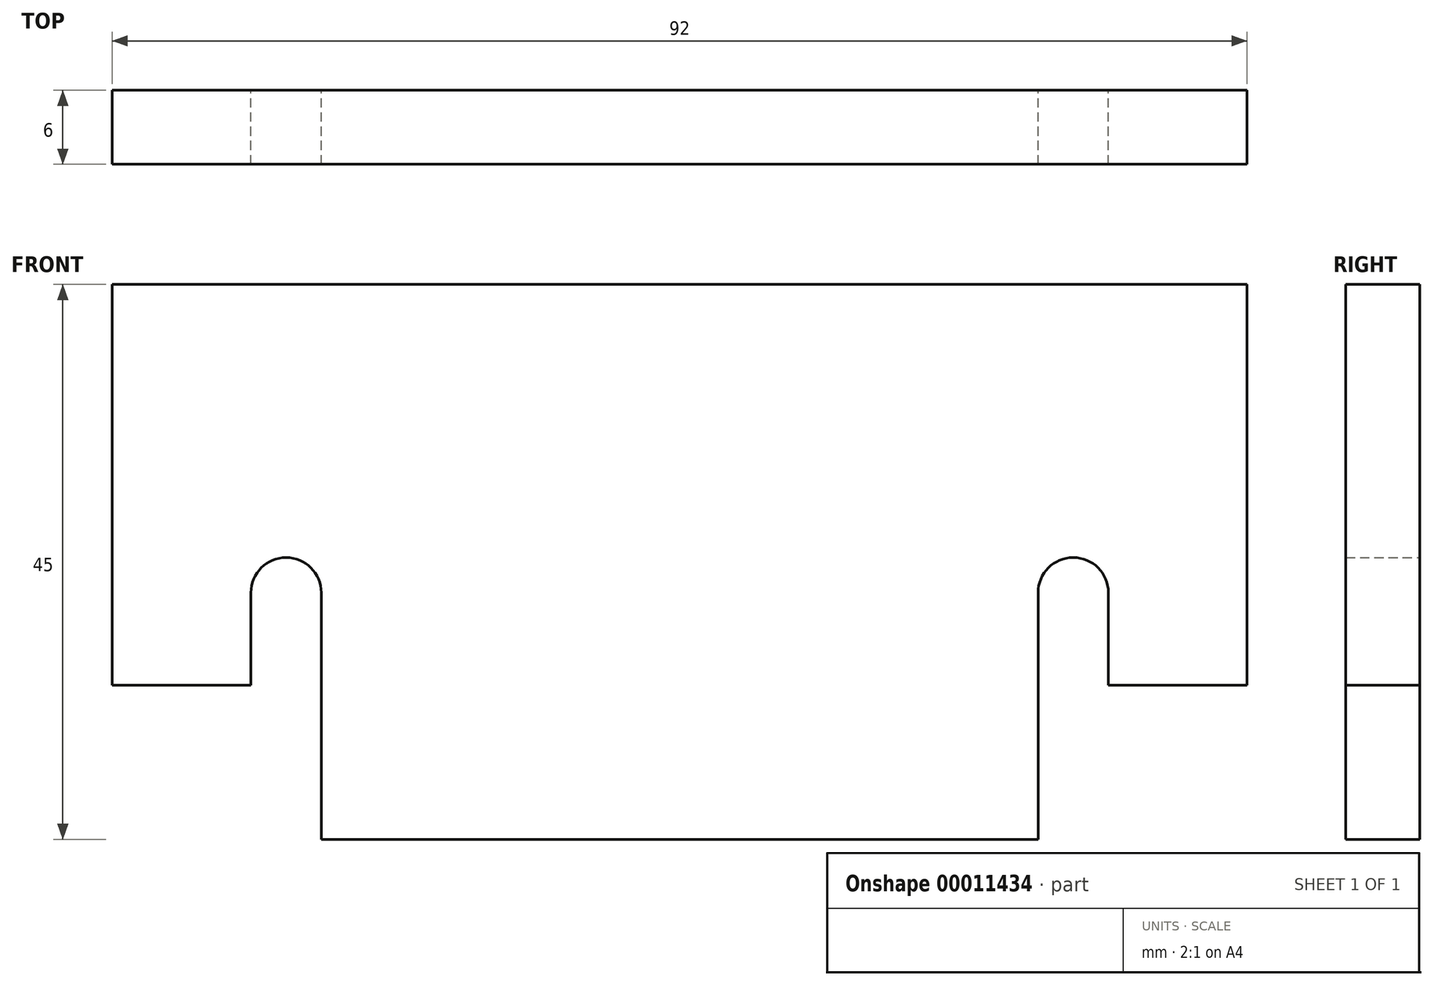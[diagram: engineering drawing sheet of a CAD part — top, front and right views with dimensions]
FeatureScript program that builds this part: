
annotation { "Feature Type Name" : "Feature", "Feature Type Description" : "" }
export const myFeature = defineFeature(function(context is Context, id is Id, definition is map)
    precondition{}
    {
        {
            var Q0;
            Q0=qCreatedBy(makeId("Front.planeOp"),FACE);
            var sketch = newSketch(context, id + "F0", { "sketchPlane" : qUnion([Q0])});
            skLineSegment(sketch, "E0.bottom", {"start": v(-46, 45) * mm, "end": v(46, 45) * mm});
            skLineSegment(sketch, "E0.left", {"start": v(-46, 45) * mm, "end": v(-46, 12.5) * mm});
            skLineSegment(sketch, "E0.right", {"start": v(46, 45) * mm, "end": v(46, 12.5) * mm});
            skLineSegment(sketch, "E1", {"start": v(-34.75, 12.5) * mm, "end": v(-34.75, 20) * mm});
            skLineSegment(sketch, "E2", {"start": v(-34.75, 20) * mm, "end": v(-29.05, 20) * mm, "construction": true});
            skLineSegment(sketch, "E3", {"start": v(-29.05, 20) * mm, "end": v(-29.05, 0) * mm});
            skLineSegment(sketch, "E4.0.MirrorCS", {"start": v(34.75, 12.5) * mm, "end": v(34.75, 20) * mm});
            skLineSegment(sketch, "E5.0.MirrorCS", {"start": v(29.05, 20) * mm, "end": v(29.05, 0) * mm});
            skLineSegment(sketch, "E6", {"start": v(-29.05, 0) * mm, "end": v(29.05, 0) * mm});
            skLineSegment(sketch, "E7", {"start": v(-46, 12.5) * mm, "end": v(-34.75, 12.5) * mm});
            skLineSegment(sketch, "E8.0.MirrorCS", {"start": v(46, 12.5) * mm, "end": v(34.75, 12.5) * mm});
            skArc(sketch, "E9", {"start": v(-29.05, 20) * mm, "mid": v(-31.9, 22.85) * mm, "end": v(-34.75, 20) * mm});
            skArc(sketch, "E10", {"start": v(34.75, 20) * mm, "mid": v(31.9, 22.85) * mm, "end": v(29.05, 20) * mm});
            skSolve(sketch);
        }
        {
            var Q0;
            Q0=makeQuery(id+"F0.imprint","IMPRINT",FACE,{"disambiguationData":[TD([[makeQuery(id+"F0.imprint","IMPRINT",EDGE,{"derivedFrom":sQuery(id+"F0.wireOp",EDGE,"E0.bottom")}),-1.0]])]});
            extrude(context, id + "F1", {"entities" : qUnion([Q0]), "depth" : 6 * mm});
        }
    });
